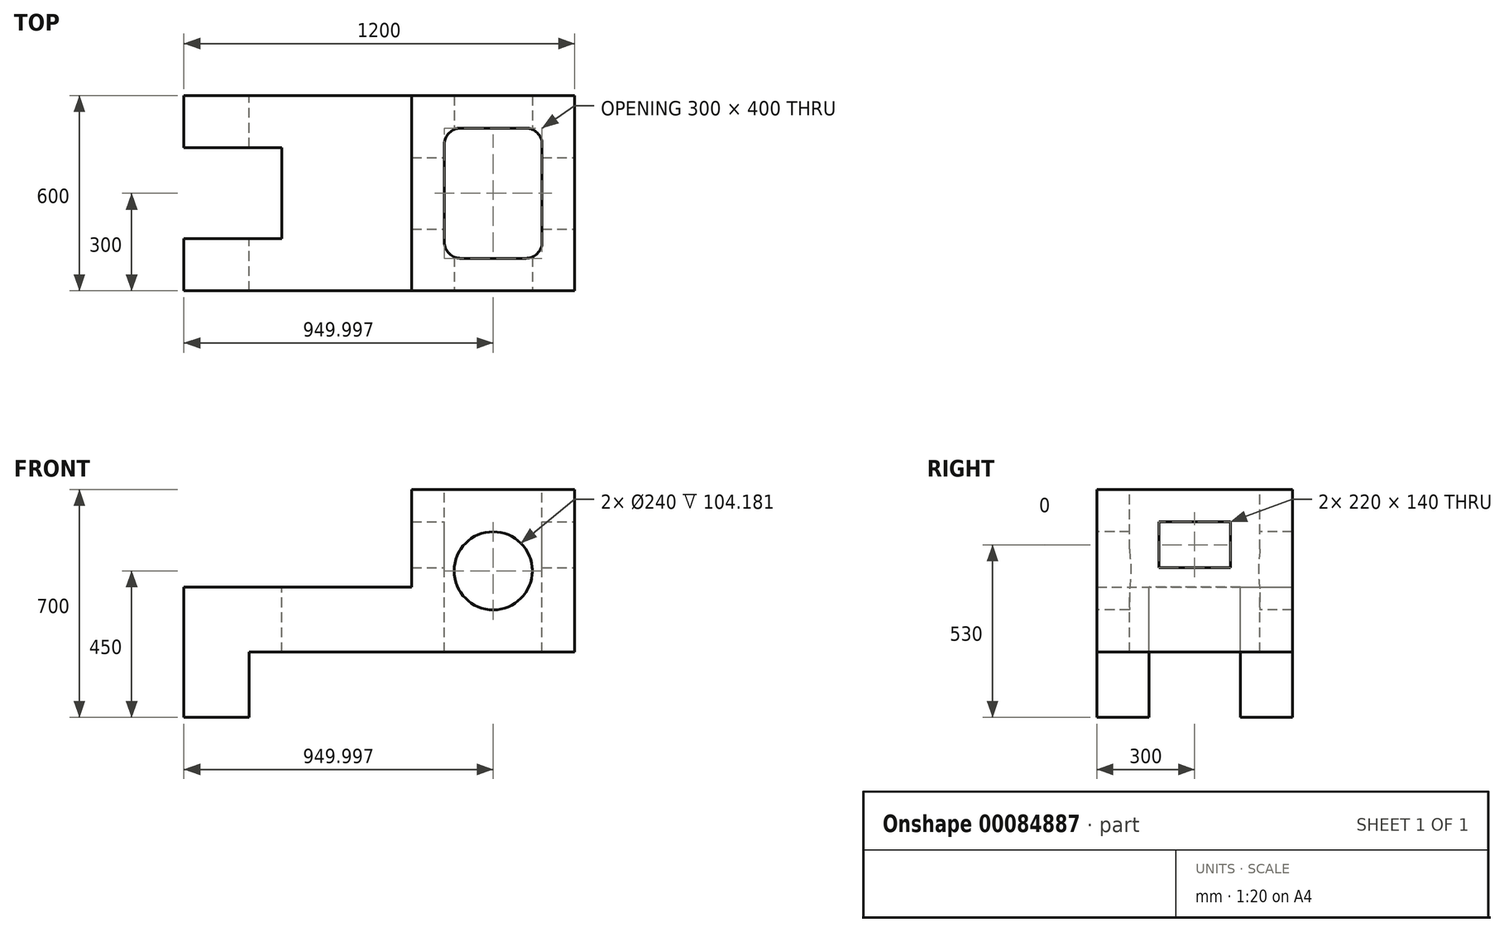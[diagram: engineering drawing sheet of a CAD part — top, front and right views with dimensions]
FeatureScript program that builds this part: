
annotation { "Feature Type Name" : "Feature", "Feature Type Description" : "" }
export const myFeature = defineFeature(function(context is Context, id is Id, definition is map)
    precondition{}
    {
        {
            var Q0;
            Q0=qCreatedBy(makeId("Front.planeOp"),FACE);
            var sketch = newSketch(context, id + "F0", { "sketchPlane" : qUnion([Q0])});
            skLineSegment(sketch, "E0", {"start": v(0, 0) * mm, "end": v(-70.95, 0) * mm});
            skLineSegment(sketch, "E1", {"start": v(-70.95, 0) * mm, "end": v(-70.95, -200) * mm});
            skLineSegment(sketch, "E2", {"start": v(-70.95, -200) * mm, "end": v(-270.95, -200) * mm});
            skLineSegment(sketch, "E3", {"start": v(-270.95, -200) * mm, "end": v(-270.95, 200) * mm});
            skLineSegment(sketch, "E4", {"start": v(-270.95, 200) * mm, "end": v(429.05, 200) * mm});
            skLineSegment(sketch, "E5", {"start": v(429.05, 200) * mm, "end": v(429.05, 500) * mm});
            skLineSegment(sketch, "E6", {"start": v(429.05, 500) * mm, "end": v(929.05, 500) * mm});
            skLineSegment(sketch, "E7", {"start": v(929.05, 500) * mm, "end": v(929.05, 0) * mm});
            skLineSegment(sketch, "E8", {"start": v(929.05, 0) * mm, "end": v(0, 0) * mm});
            skSolve(sketch);
        }
        {
            var Q0;
            Q0 = qSketchRegion(id + "F0", true);
            extrude(context, id + "F1", {"entities" : qUnion([Q0]), "depth" : 600 * mm});
        }
        {
            var Q0;
            Q0=makeQuery(id+"F1.opExtrude","SWEPT_FACE",FACE,{"disambiguationData":[OSD([sQuery(id+"F0.wireOp",EDGE,"E4")])]});
            var sketch = newSketch(context, id + "F2", { "sketchPlane" : qUnion([Q0])});
            skLineSegment(sketch, "E9.bottom", {"start": v(-570.95, -160) * mm, "end": v(29.05, -160) * mm});
            skLineSegment(sketch, "E9.top", {"start": v(-570.95, -440) * mm, "end": v(29.05, -440) * mm});
            skLineSegment(sketch, "E9.left", {"start": v(-570.95, -160) * mm, "end": v(-570.95, -440) * mm});
            skLineSegment(sketch, "E9.right", {"start": v(29.05, -160) * mm, "end": v(29.05, -440) * mm});
            skPoint(sketch, "E9.middle", {"position": v(-270.95, -300) * mm});
            skSolve(sketch);
        }
        {
            var Q0;
            Q0 = qSketchRegion(id + "F2", true);
            extrude(context, id + "F3", {"entities" : qUnion([Q0]), "operationType" : NewBodyOperationType.REMOVE, "endBound" : BoundingType.THROUGH_ALL, "oppositeDirection" : true, "depth" : 25 * mm});
        }
        {
            var Q0;
            Q0=makeQuery(id+"F1.opExtrude","SWEPT_FACE",FACE,{"disambiguationData":[OSD([sQuery(id+"F0.wireOp",EDGE,"E6")])]});
            var sketch = newSketch(context, id + "F4", { "sketchPlane" : qUnion([Q0])});
            skLineSegment(sketch, "E10.bottom", {"start": v(579.05, -500) * mm, "end": v(779.05, -500) * mm});
            skLineSegment(sketch, "E10.top", {"start": v(579.05, -100) * mm, "end": v(779.05, -100) * mm});
            skLineSegment(sketch, "E10.left", {"start": v(529.05, -450) * mm, "end": v(529.05, -150) * mm});
            skLineSegment(sketch, "E10.right", {"start": v(829.05, -450) * mm, "end": v(829.05, -150) * mm});
            skPoint(sketch, "E10.middle", {"position": v(679.05, -300) * mm});
            skPoint(sketch, "E10.middle.positionSnap0", {"position": v(929.05, -300) * mm});
            skPoint(sketch, "E10.middle.positionSnap1", {"position": v(679.05, 0) * mm});
            skPoint(sketch, "E10.centerSnap0", {"position": v(929.05, -300) * mm});
            skPoint(sketch, "E10.centerSnap1", {"position": v(679.05, 0) * mm});
            skPoint(sketch, "E11.visualSharp", {"position": v(829.05, -100) * mm});
            skArc(sketch, "E11.filletArc", {"start": v(829.05, -150) * mm, "mid": v(814.4, -114.64) * mm, "end": v(779.05, -100) * mm});
            skPoint(sketch, "E12.visualSharp", {"position": v(829.05, -500) * mm});
            skArc(sketch, "E12.filletArc", {"start": v(779.05, -500) * mm, "mid": v(814.4, -485.36) * mm, "end": v(829.05, -450) * mm});
            skPoint(sketch, "E13.visualSharp", {"position": v(529.05, -100) * mm});
            skArc(sketch, "E13.filletArc", {"start": v(579.05, -100) * mm, "mid": v(543.7, -114.64) * mm, "end": v(529.05, -150) * mm});
            skPoint(sketch, "E14.visualSharp", {"position": v(529.05, -500) * mm});
            skArc(sketch, "E14.filletArc", {"start": v(529.05, -450) * mm, "mid": v(543.7, -485.36) * mm, "end": v(579.05, -500) * mm});
            skSolve(sketch);
        }
        {
            var Q0;
            Q0 = qSketchRegion(id + "F4", true);
            extrude(context, id + "F5", {"entities" : qUnion([Q0]), "operationType" : NewBodyOperationType.REMOVE, "endBound" : BoundingType.THROUGH_ALL, "oppositeDirection" : true, "depth" : 25 * mm});
        }
        {
            var Q0;
            Q0=makeQuery(id+"F1.opExtrude","CAP_FACE",FACE,{"disambiguationData":[OSD([sQuery(id+"F0.wireOp",EDGE,"E0"),sQuery(id+"F0.wireOp",EDGE,"E1"),sQuery(id+"F0.wireOp",EDGE,"E2"),sQuery(id+"F0.wireOp",EDGE,"E3"),sQuery(id+"F0.wireOp",EDGE,"E4"),sQuery(id+"F0.wireOp",EDGE,"E5"),sQuery(id+"F0.wireOp",EDGE,"E6"),sQuery(id+"F0.wireOp",EDGE,"E7"),sQuery(id+"F0.wireOp",EDGE,"E8")])],"isStart":false});
            var sketch = newSketch(context, id + "F6", { "sketchPlane" : qUnion([Q0])});
            skCircle(sketch, "E15", {"center": v(679.05, 250) * mm, "radius": 120 * mm});
            skPoint(sketch, "E15.centerSnap0", {"position": v(929.05, 250) * mm});
            skPoint(sketch, "E15.centerSnap1", {"position": v(679.05, 500) * mm});
            skSolve(sketch);
        }
        {
            var Q0;
            Q0 = qSketchRegion(id + "F6", true);
            extrude(context, id + "F7", {"entities" : qUnion([Q0]), "operationType" : NewBodyOperationType.REMOVE, "endBound" : BoundingType.THROUGH_ALL, "oppositeDirection" : true, "depth" : 25 * mm});
        }
        {
            var Q0;
            Q0=makeQuery(id+"F1.opExtrude","SWEPT_FACE",FACE,{"disambiguationData":[OSD([sQuery(id+"F0.wireOp",EDGE,"E7")])]});
            var sketch = newSketch(context, id + "F8", { "sketchPlane" : qUnion([Q0])});
            skLineSegment(sketch, "E16.bottom", {"start": v(-410, 260) * mm, "end": v(-190, 260) * mm});
            skLineSegment(sketch, "E16.top", {"start": v(-410, 400) * mm, "end": v(-190, 400) * mm});
            skLineSegment(sketch, "E16.left", {"start": v(-410, 260) * mm, "end": v(-410, 400) * mm});
            skLineSegment(sketch, "E16.right", {"start": v(-190, 260) * mm, "end": v(-190, 400) * mm});
            skPoint(sketch, "E16.middle", {"position": v(-300, 330) * mm});
            skPoint(sketch, "E16.middle.positionSnap0", {"position": v(-300, 500) * mm});
            skPoint(sketch, "E16.centerSnap0", {"position": v(-300, 500) * mm});
            skSolve(sketch);
        }
        {
            var Q0;
            Q0 = qSketchRegion(id + "F8", true);
            extrude(context, id + "F9", {"entities" : qUnion([Q0]), "operationType" : NewBodyOperationType.REMOVE, "endBound" : BoundingType.THROUGH_ALL, "oppositeDirection" : true, "depth" : 25 * mm});
        }
    });
